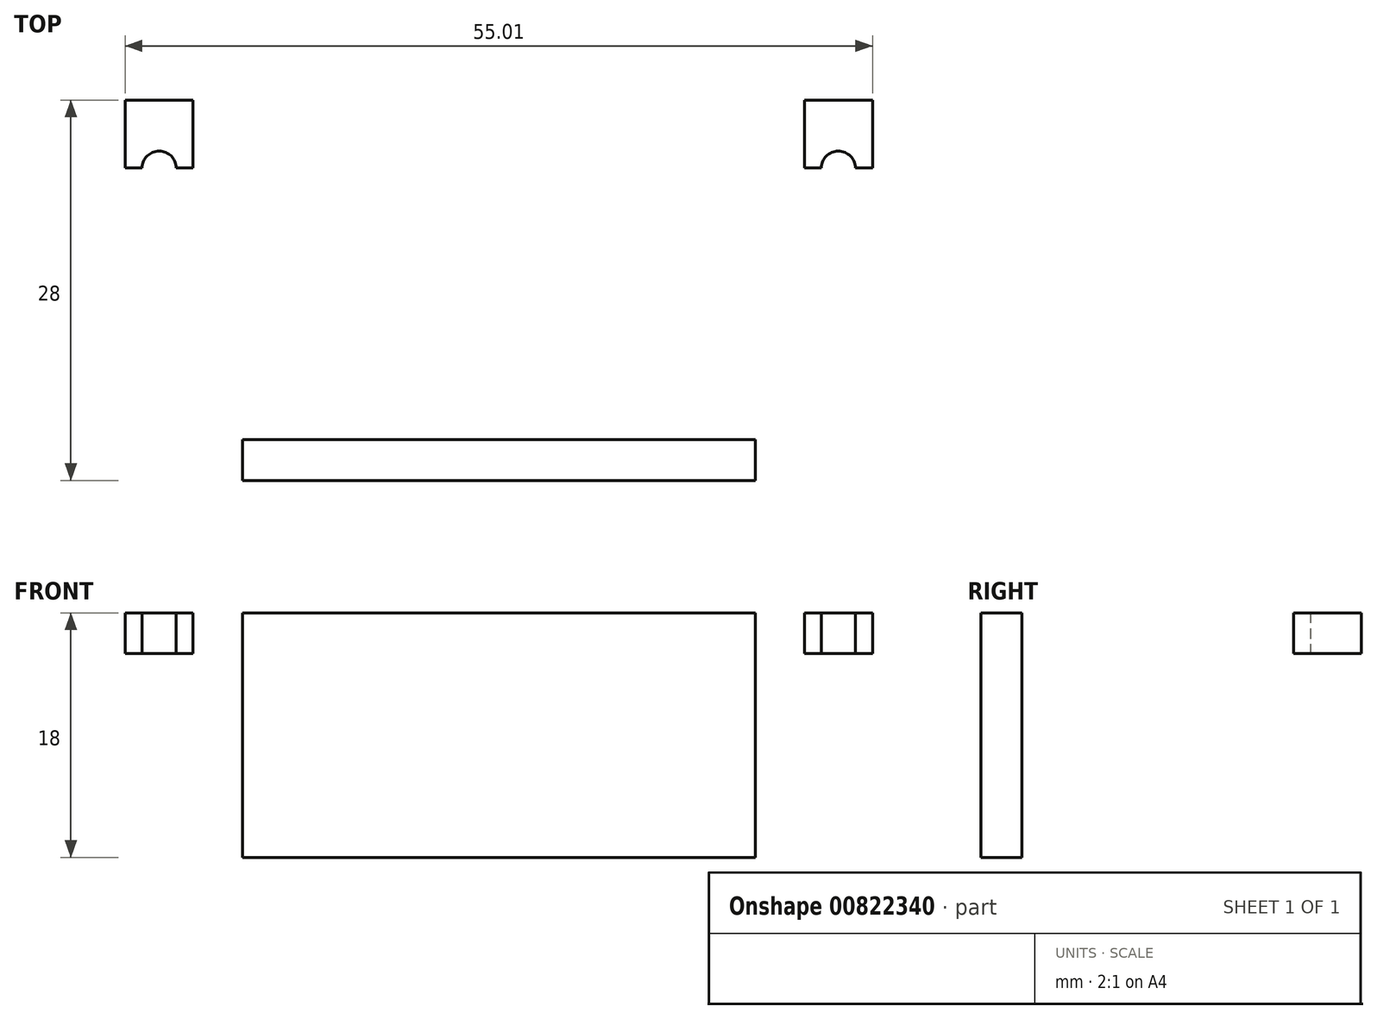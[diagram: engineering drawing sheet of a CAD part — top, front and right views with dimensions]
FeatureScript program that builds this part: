
annotation { "Feature Type Name" : "Feature", "Feature Type Description" : "" }
export const myFeature = defineFeature(function(context is Context, id is Id, definition is map)
    precondition{}
    {
        {
            var Q0;
            Q0=qCreatedBy(makeId("Top.planeOp"),FACE);
            var sketch = newSketch(context, id + "F0", { "sketchPlane" : qUnion([Q0])});
            skCircle(sketch, "E0", {"center": v(0, 0) * mm, "radius": 25 * mm, "construction": true});
            skCircle(sketch, "E1", {"center": v(-25, 0) * mm, "radius": 1.25 * mm});
            skCircle(sketch, "E2", {"center": v(25, 0) * mm, "radius": 1.25 * mm});
            skCircle(sketch, "E3", {"center": v(0, 0) * mm, "radius": 22.5 * mm});
            skCircle(sketch, "E4", {"center": v(0, 0) * mm, "radius": 27.5 * mm});
            skLineSegment(sketch, "E5.bottom", {"start": v(-27.5, 0) * mm, "end": v(27.5, 0) * mm});
            skLineSegment(sketch, "E5.top", {"start": v(-27.5, 5) * mm, "end": v(27.5, 5) * mm});
            skLineSegment(sketch, "E5.left", {"start": v(-27.5, 0) * mm, "end": v(-27.5, 5) * mm});
            skLineSegment(sketch, "E5.right", {"start": v(27.5, 0) * mm, "end": v(27.5, 5) * mm});
            skLineSegment(sketch, "E6", {"start": v(-22.5, 0) * mm, "end": v(-22.5, 5) * mm});
            skLineSegment(sketch, "E7", {"start": v(22.5, 0) * mm, "end": v(22.5, 5) * mm});
            skLineSegment(sketch, "E8", {"start": v(0, 0) * mm, "end": v(0, -20) * mm, "construction": true});
            skLineSegment(sketch, "E9", {"start": v(0, -20) * mm, "end": v(-18.87, -20) * mm});
            skLineSegment(sketch, "E10", {"start": v(-18.87, -20) * mm, "end": v(-18.87, -23) * mm});
            skLineSegment(sketch, "E11", {"start": v(0, -20) * mm, "end": v(18.87, -20) * mm});
            skLineSegment(sketch, "E12", {"start": v(18.87, -20) * mm, "end": v(18.87, -23) * mm});
            skLineSegment(sketch, "E13", {"start": v(18.87, -23) * mm, "end": v(-18.87, -23) * mm});
            skSolve(sketch);
        }
        {
            var Q0;
            {var subQ0=sQuery(id+"F0.wireOp",EDGE,"E7");Q0=makeQuery(id+"F0.imprint","IMPRINT",FACE,{"disambiguationData":[TD([[makeQuery(id+"F0.imprint","IMPRINT",EDGE,{"derivedFrom":subQ0}),-1.0]])]});}
            var Q1;
            {var subQ5=sQuery(id+"F0.wireOp",EDGE,"E5.right");Q1=makeQuery(id+"F0.imprint","IMPRINT",FACE,{"disambiguationData":[TD([[makeQuery(id+"F0.imprint","IMPRINT",EDGE,{"derivedFrom":subQ5}),1.0]])]});}
            var Q2;
            {var subQ0=sQuery(id+"F0.wireOp",EDGE,"E5.bottom");var subQ9=sQuery(id+"F0.wireOp",EDGE,"E1");var subQ12=makeQuery(id+"F0.imprint","INTERSECT",VERTEX,{"disambiguationData":[OD(0.0)],"derivedFrom":[subQ9,subQ0]});Q2=makeQuery(id+"F0.imprint","IMPRINT",FACE,{"disambiguationData":[TD([[makeQuery(id+"F0.imprint","IMPRINT",EDGE,{"disambiguationData":[TD([[subQ12,-1.0]])],"derivedFrom":subQ9}),-1.0]])]});}
            var Q3;
            {var subQ0=sQuery(id+"F0.wireOp",EDGE,"E6");Q3=makeQuery(id+"F0.imprint","IMPRINT",FACE,{"disambiguationData":[TD([[makeQuery(id+"F0.imprint","IMPRINT",EDGE,{"derivedFrom":subQ0}),1.0]])]});}
            var Q4;
            {var subQ0=sQuery(id+"F0.wireOp",EDGE,"E5.left");Q4=makeQuery(id+"F0.imprint","IMPRINT",FACE,{"disambiguationData":[TD([[makeQuery(id+"F0.imprint","IMPRINT",EDGE,{"derivedFrom":subQ0}),-1.0]])]});}
            var Q5;
            {var subQ0=sQuery(id+"F0.wireOp",EDGE,"E5.bottom");var subQ3=sQuery(id+"F0.wireOp",EDGE,"E2");var subQ4=makeQuery(id+"F0.imprint","INTERSECT",VERTEX,{"disambiguationData":[OD(0.0)],"derivedFrom":[subQ3,subQ0]});Q5=makeQuery(id+"F0.imprint","IMPRINT",FACE,{"disambiguationData":[TD([[makeQuery(id+"F0.imprint","IMPRINT",EDGE,{"disambiguationData":[TD([[subQ4,-1.0]])],"derivedFrom":subQ3}),-1.0]])]});}
            extrude(context, id + "F1", {"entities" : qUnion([Q0, Q1, Q2, Q3, Q4, Q5]), "depth" : 3 * mm, "offsetDistance" : 25 * mm});
        }
        {
            var Q0;
            {var subQ5=sQuery(id+"F0.wireOp",EDGE,"E9");var subQ7=sQuery(id+"F0.wireOp",EDGE,"E3");var subQ8=makeQuery(id+"F0.imprint","INTERSECT",VERTEX,{"derivedFrom":[subQ7,subQ5]});Q0=makeQuery(id+"F0.imprint","IMPRINT",FACE,{"disambiguationData":[TD([[makeQuery(id+"F0.imprint","IMPRINT",EDGE,{"disambiguationData":[TD([[subQ8,-1.0]])],"derivedFrom":subQ7}),-1.0]])]});}
            var Q1;
            {var subQ0=sQuery(id+"F0.wireOp",EDGE,"E10");Q1=makeQuery(id+"F0.imprint","IMPRINT",FACE,{"disambiguationData":[TD([[makeQuery(id+"F0.imprint","IMPRINT",EDGE,{"derivedFrom":subQ0}),1.0]])]});}
            var Q2;
            {var subQ0=sQuery(id+"F0.wireOp",EDGE,"E12");Q2=makeQuery(id+"F0.imprint","IMPRINT",FACE,{"disambiguationData":[TD([[makeQuery(id+"F0.imprint","IMPRINT",EDGE,{"derivedFrom":subQ0}),-1.0]])]});}
            var Q3;
            {var subQ0=sQuery(id+"F0.wireOp",EDGE,"E9");var subQ1=sQuery(id+"F0.wireOp",EDGE,"E3");var subQ2=makeQuery(id+"F0.imprint","INTERSECT",VERTEX,{"derivedFrom":[subQ1,subQ0]});Q3=makeQuery(id+"F0.imprint","IMPRINT",FACE,{"disambiguationData":[TD([[makeQuery(id+"F0.imprint","IMPRINT",EDGE,{"disambiguationData":[TD([[subQ2,-1.0]])],"derivedFrom":subQ1}),1.0]])]});}
            extrude(context, id + "F2", {"entities" : qUnion([Q0, Q1, Q2, Q3]), "oppositeDirection" : true, "depth" : 15 * mm, "offsetDistance" : 25 * mm, "hasSecondDirection" : true, "secondDirectionOppositeDirection" : false, "secondDirectionDepth" : 3 * mm});
        }
    });
